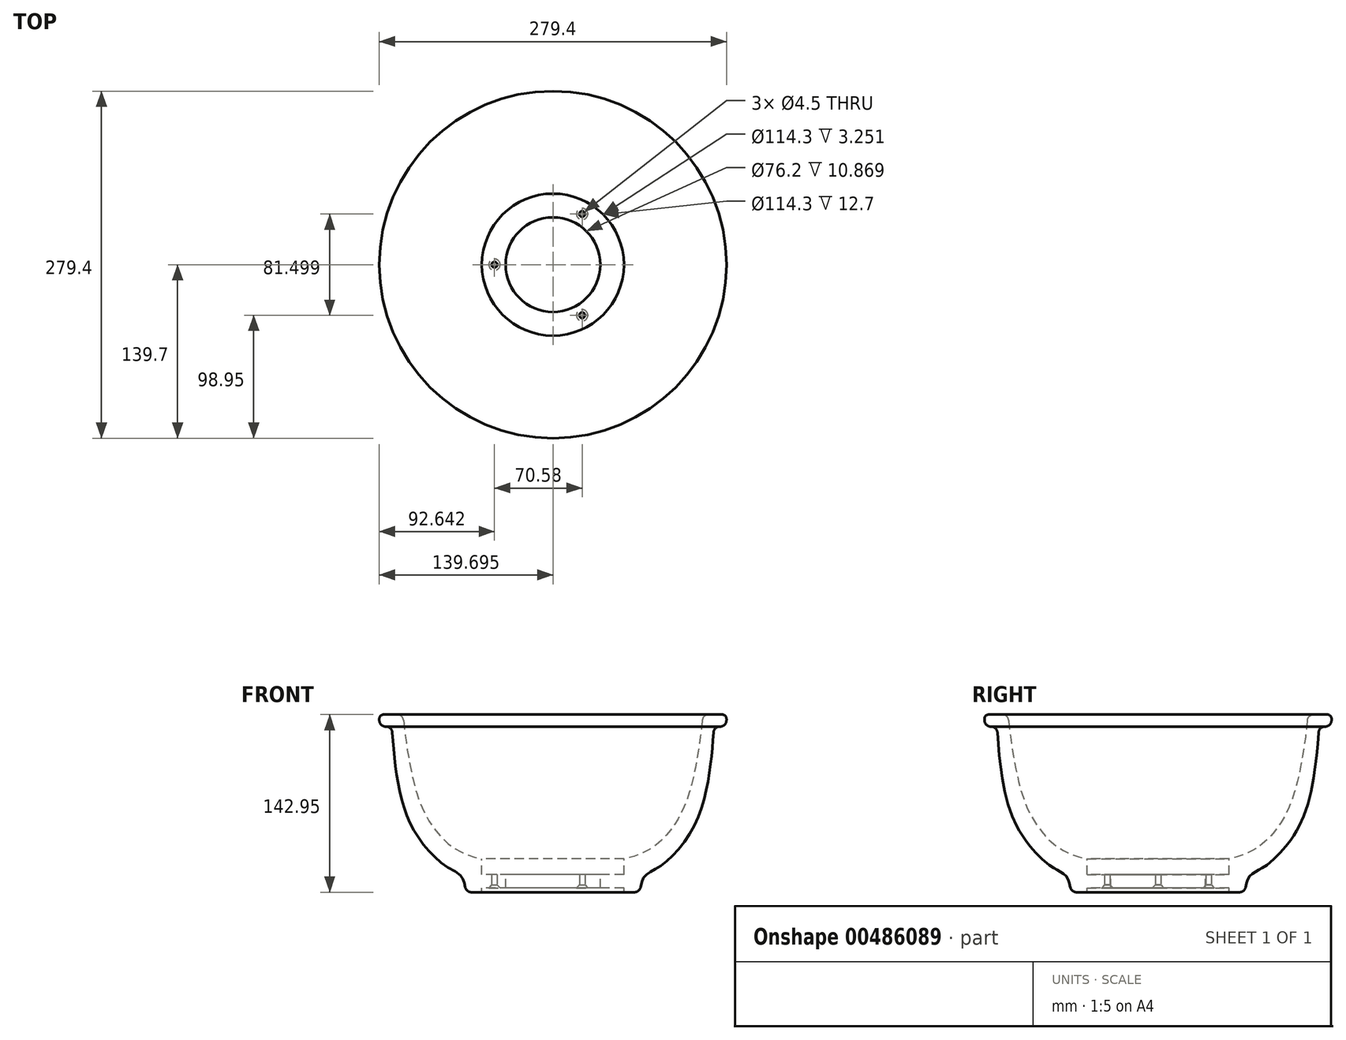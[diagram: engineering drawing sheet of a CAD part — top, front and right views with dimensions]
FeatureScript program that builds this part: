
annotation { "Feature Type Name" : "Feature", "Feature Type Description" : "" }
export const myFeature = defineFeature(function(context is Context, id is Id, definition is map)
    precondition{}
    {
        {
            var Q0;
            Q0=qCreatedBy(makeId("Front.planeOp"),FACE);
            var sketch = newSketch(context, id + "F0", { "sketchPlane" : qUnion([Q0])});
            skLineSegment(sketch, "E0", {"start": v(19.97, -51.7) * mm, "end": v(19.97, -32.65) * mm});
            skLineSegment(sketch, "E1", {"start": v(19.97, -32.65) * mm, "end": v(0.92, -32.65) * mm});
            skLineSegment(sketch, "E2", {"start": v(0.92, -32.65) * mm, "end": v(0.92, -19.95) * mm});
            skLineSegment(sketch, "E3", {"start": v(-62.58, 96.18) * mm, "end": v(-81.63, 96.18) * mm});
            skLineSegment(sketch, "E4", {"start": v(-81.63, 96.18) * mm, "end": v(-81.63, 86.53) * mm});
            skLineSegment(sketch, "E5", {"start": v(-81.63, 86.53) * mm, "end": v(-71.47, 86.53) * mm});
            skLineSegment(sketch, "E6", {"start": v(-11.78, -46.77) * mm, "end": v(0.92, -46.77) * mm});
            skLineSegment(sketch, "E7", {"start": v(0.92, -46.77) * mm, "end": v(0.92, -43.52) * mm});
            skLineSegment(sketch, "E8", {"start": v(0.92, -43.52) * mm, "end": v(19.97, -43.52) * mm});
            skLineSegment(sketch, "E9", {"start": v(58.07, -53.75) * mm, "end": v(58.07, -31.18) * mm, "construction": true});
            skLineSegment(sketch, "E10", {"start": v(58.07, 95.82) * mm, "end": v(58.07, -31.18) * mm, "construction": true});
            skFitSpline(sketch, "E11", {"points": [v(-62.58, 96.18) * mm, v(-60.4, 76.3) * mm, v(-51.05, 31.21) * mm, v(-35.65, 2.1) * mm, v(0.92, -19.95) * mm], "startDerivative": vector(7.22, -90.77) * mm, "endDerivative": vector(206.92, -41.9) * mm});
            skFitSpline(sketch, "E12", {"points": [v(-11.78, -46.77) * mm, v(-15.41, -34.36) * mm, v(-28.26, -25.81) * mm, v(-55.45, 6.07) * mm, v(-68.1, 50.84) * mm, v(-71.47, 86.53) * mm], "startDerivative": vector(-18.47, 92.54) * mm, "endDerivative": vector(-9.11, 154.2) * mm});
            skLineSegment(sketch, "E13", {"start": v(58.07, -53.75) * mm, "end": v(58.07, 9.75) * mm, "construction": true});
            skPoint(sketch, "E14", {"position": v(58.07, -19.26) * mm});
            skSolve(sketch);
        }
        {
            var Q0;
            {var subQ1=sQuery(id+"F0.wireOp",EDGE,"E1");Q0=makeQuery(id+"F0.imprint","IMPRINT",FACE,{"disambiguationData":[TD([[makeQuery(id+"F0.imprint","IMPRINT",EDGE,{"derivedFrom":subQ1}),1.0]])]});}
            var Q1;
            Q1=sQuery(id+"F0.wireOp",EDGE,"E10");
            revolve(context, id + "F1", {"entities" : qUnion([Q0]), "axis" : qUnion([Q1]), "revolveType" : RevolveType.FULL});
        }
        {
            var Q0;
            Q0=makeQuery(id+"F1.opRevolve","SWEPT_EDGE",EDGE,{"disambiguationData":[OSD([sQuery(id+"F0.wireOp",EDGE,"E4"),sQuery(id+"F0.wireOp",EDGE,"E5")])]});
            var Q1;
            Q1=makeQuery(id+"F1.opRevolve","SWEPT_EDGE",EDGE,{"disambiguationData":[OSD([sQuery(id+"F0.wireOp",EDGE,"E5"),sQuery(id+"F0.wireOp",EDGE,"E12")])]});
            var Q2;
            Q2=makeQuery(id+"F1.opRevolve","SWEPT_EDGE",EDGE,{"disambiguationData":[OSD([sQuery(id+"F0.wireOp",EDGE,"E3"),sQuery(id+"F0.wireOp",EDGE,"E11")])]});
            var Q3;
            Q3=makeQuery(id+"F1.opRevolve","SWEPT_EDGE",EDGE,{"disambiguationData":[OSD([sQuery(id+"F0.wireOp",EDGE,"E6"),sQuery(id+"F0.wireOp",EDGE,"E12")])]});
            fillet(context, id + "F2", {"entities" : qUnion([Q0, Q1, Q2, Q3]), "radius" : 5.08 * mm, "tangentPropagation" : true, "allowEdgeOverflow" : false});
        }
        {
            var Q0;
            Q0=makeQuery(id+"F1.opRevolve","SWEPT_EDGE",EDGE,{"disambiguationData":[OSD([sQuery(id+"F0.wireOp",EDGE,"E3"),sQuery(id+"F0.wireOp",EDGE,"E4")])]});
            fillet(context, id + "F3", {"entities" : qUnion([Q0]), "radius" : 3.25 * mm, "tangentPropagation" : true, "allowEdgeOverflow" : false});
        }
        {
            var Q0;
            Q0=makeQuery(id+"F1.opRevolve","SWEPT_FACE",FACE,{"disambiguationData":[OSD([sQuery(id+"F0.wireOp",EDGE,"E8")])]});
            var sketch = newSketch(context, id + "F4", { "sketchPlane" : qUnion([Q0])});
            skCircle(sketch, "E15", {"center": v(58.07, 0) * mm, "radius": 47.05 * mm, "construction": true});
            skPoint(sketch, "E16", {"position": v(11.01, 0) * mm});
            skPoint(sketch, "E17.1.0", {"position": v(81.6, -40.75) * mm});
            skPoint(sketch, "E17.2.0", {"position": v(81.6, 40.75) * mm});
            skSolve(sketch);
        }
        {
            var Q0;
            Q0=sQuery(id+"F4.wireOp",VERTEX,"E16");
            var Q1;
            Q1=sQuery(id+"F4.wireOp",VERTEX,"E17.2.0");
            var Q2;
            Q2=sQuery(id+"F4.wireOp",VERTEX,"E17.1.0");
            var Q3;
            Q3=makeQuery(id+"F1.opRevolve","SWEPT_BODY",BODY,{"disambiguationData":[OSD([sQuery(id+"F0.wireOp",EDGE,"E0"),sQuery(id+"F0.wireOp",EDGE,"E1"),sQuery(id+"F0.wireOp",EDGE,"E2"),sQuery(id+"F0.wireOp",EDGE,"E3"),sQuery(id+"F0.wireOp",EDGE,"E4"),sQuery(id+"F0.wireOp",EDGE,"E5"),sQuery(id+"F0.wireOp",EDGE,"E6"),sQuery(id+"F0.wireOp",EDGE,"E7"),sQuery(id+"F0.wireOp",EDGE,"E8"),sQuery(id+"F0.wireOp",EDGE,"E11"),sQuery(id+"F0.wireOp",EDGE,"E12")])]});
            hole(context, id + "F5", {"style" : HoleStyle.C_SINK, "endStyle" : HoleEndStyle.THROUGH, "standardTappedOrClearance" : lookupTablePath({ "standard" : "ANSI", "fit" : "Normal (ASME)", "size" : "#8", "type" : "Clearance" }), "standardBlindInLast" : lookupTablePath({ "fit" : "Free", "standard" : "ANSI", "size" : "#8", "type" : "Clearance" }), "holeDiameter" : 4.5 * mm, "cSinkDiameter" : 9.12 * mm, "cSinkAngle" : 82 * degree, "isTappedThrough" : true, "tappedDepth" : 12.7 * mm, "tapClearance" : 3, "locations" : qUnion([Q0, Q1, Q2]), "scope" : qUnion([Q3])});
        }
    });
